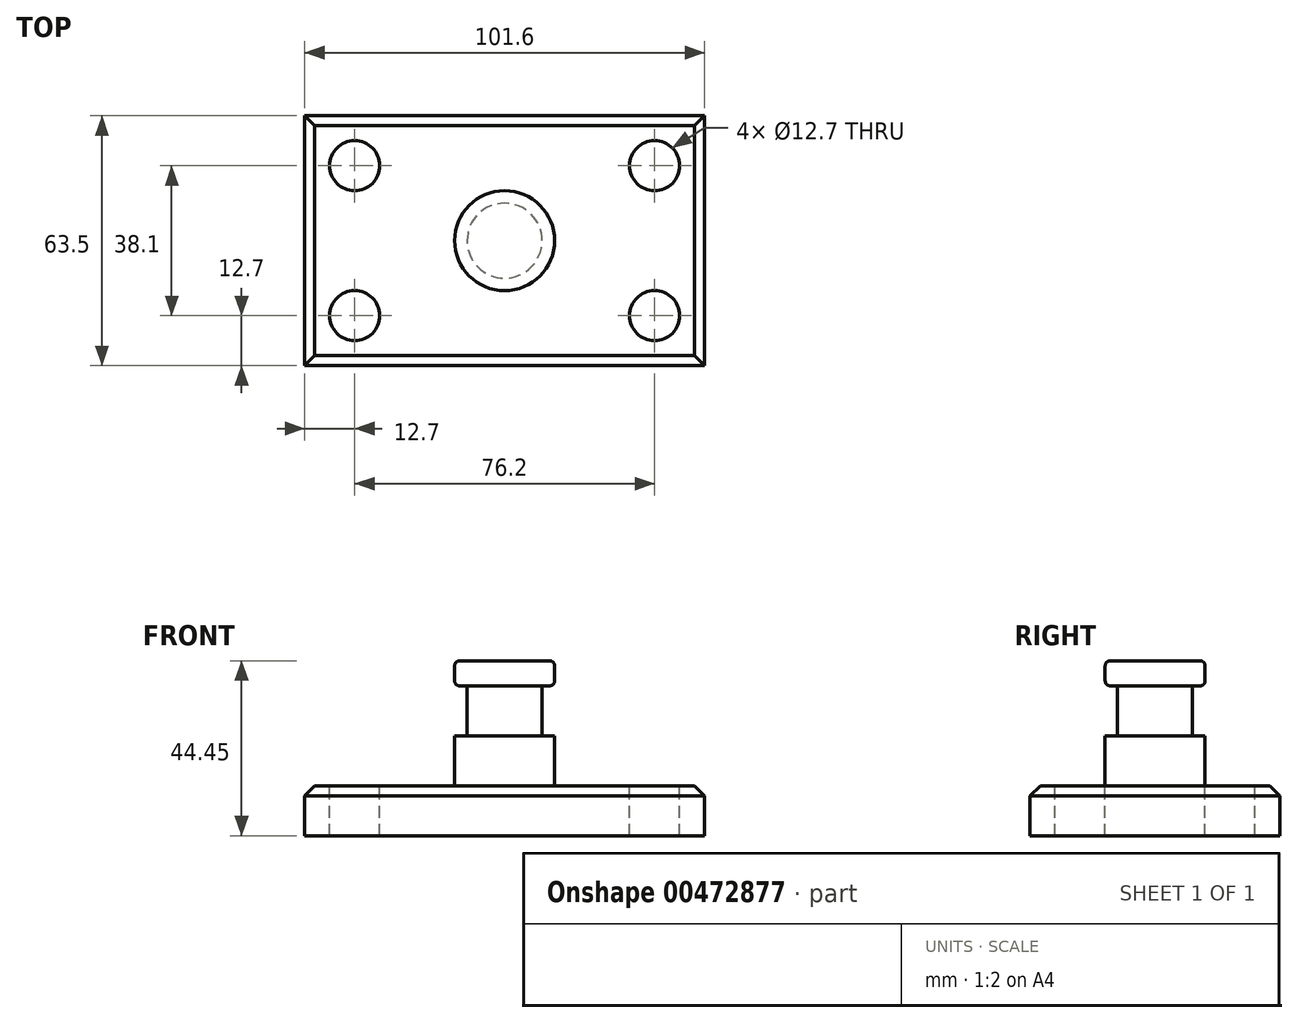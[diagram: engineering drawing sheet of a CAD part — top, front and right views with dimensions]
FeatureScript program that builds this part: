
annotation { "Feature Type Name" : "Feature", "Feature Type Description" : "" }
export const myFeature = defineFeature(function(context is Context, id is Id, definition is map)
    precondition{}
    {
        {
            var Q0;
            Q0=qCreatedBy(makeId("Top.planeOp"),FACE);
            var sketch = newSketch(context, id + "F0", { "sketchPlane" : qUnion([Q0])});
            skLineSegment(sketch, "E0.bottom", {"start": v(50.8, -31.75) * mm, "end": v(-50.8, -31.75) * mm});
            skLineSegment(sketch, "E0.top", {"start": v(50.8, 31.75) * mm, "end": v(-50.8, 31.75) * mm});
            skLineSegment(sketch, "E0.left", {"start": v(50.8, -31.75) * mm, "end": v(50.8, 31.75) * mm});
            skLineSegment(sketch, "E0.right", {"start": v(-50.8, -31.75) * mm, "end": v(-50.8, 31.75) * mm});
            skPoint(sketch, "E0.middle", {"position": v(0, 0) * mm});
            skSolve(sketch);
        }
        {
            var Q0;
            Q0=makeQuery(id+"F0.imprint","IMPRINT",FACE,{"disambiguationData":[TD([[makeQuery(id+"F0.imprint","IMPRINT",EDGE,{"derivedFrom":sQuery(id+"F0.wireOp",EDGE,"E0.bottom")}),-1.0]])]});
            extrude(context, id + "F1", {"entities" : qUnion([Q0]), "depth" : 12.7 * mm});
        }
        {
            var Q0;
            Q0=makeQuery(id+"F1.opExtrude","CAP_FACE",FACE,{"disambiguationData":[OSD([sQuery(id+"F0.wireOp",EDGE,"E0.bottom"),sQuery(id+"F0.wireOp",EDGE,"E0.top"),sQuery(id+"F0.wireOp",EDGE,"E0.left"),sQuery(id+"F0.wireOp",EDGE,"E0.right")])],"isStart":false});
            var sketch = newSketch(context, id + "F2", { "sketchPlane" : qUnion([Q0])});
            skCircle(sketch, "E1", {"center": v(-38.1, 19.05) * mm, "radius": 6.35 * mm});
            skCircle(sketch, "E2", {"center": v(-38.1, -19.05) * mm, "radius": 6.35 * mm});
            skCircle(sketch, "E3.MirrorC", {"center": v(38.1, 19.05) * mm, "radius": 6.35 * mm});
            skCircle(sketch, "E4.MirrorC", {"center": v(38.1, -19.05) * mm, "radius": 6.35 * mm});
            skSolve(sketch);
        }
        {
            var Q0;
            Q0 = qSketchRegion(id + "F2", true);
            extrude(context, id + "F3", {"entities" : qUnion([Q0]), "operationType" : NewBodyOperationType.REMOVE, "endBound" : BoundingType.THROUGH_ALL, "oppositeDirection" : true, "depth" : 25.4 * mm});
        }
        {
            var Q0;
            Q0=qCreatedBy(makeId("Front.planeOp"),FACE);
            var sketch = newSketch(context, id + "F4", { "sketchPlane" : qUnion([Q0])});
            skLineSegment(sketch, "E5.bottom", {"start": v(0, 12.7) * mm, "end": v(12.7, 12.7) * mm});
            skLineSegment(sketch, "E5.top", {"start": v(0, 44.45) * mm, "end": v(12.7, 44.45) * mm});
            skLineSegment(sketch, "E5.left", {"start": v(0, 12.7) * mm, "end": v(0, 44.45) * mm});
            skLineSegment(sketch, "E5.right", {"start": v(12.7, 12.7) * mm, "end": v(12.7, 44.45) * mm});
            skSolve(sketch);
        }
        {
            var Q0;
            Q0=makeQuery(id+"F4.imprint","IMPRINT",FACE,{"disambiguationData":[TD([[makeQuery(id+"F4.imprint","IMPRINT",EDGE,{"derivedFrom":sQuery(id+"F4.wireOp",EDGE,"E5.bottom")}),1.0]])]});
            var Q1;
            Q1=sQuery(id+"F4.wireOp",EDGE,"E5.left");
            revolve(context, id + "F5", {"operationType" : NewBodyOperationType.ADD, "entities" : qUnion([Q0]), "axis" : qUnion([Q1]), "revolveType" : RevolveType.FULL});
        }
        {
            var Q0;
            Q0=qCreatedBy(makeId("Front.planeOp"),FACE);
            var sketch = newSketch(context, id + "F6", { "sketchPlane" : qUnion([Q0])});
            skLineSegment(sketch, "E6.bottom", {"start": v(12.7, 38.1) * mm, "end": v(9.52, 38.1) * mm});
            skLineSegment(sketch, "E6.top", {"start": v(12.7, 25.4) * mm, "end": v(9.52, 25.4) * mm});
            skLineSegment(sketch, "E6.left", {"start": v(12.7, 38.1) * mm, "end": v(12.7, 25.4) * mm});
            skLineSegment(sketch, "E6.right", {"start": v(9.52, 38.1) * mm, "end": v(9.52, 25.4) * mm});
            skSolve(sketch);
        }
        {
            var Q0;
            Q0 = qSketchRegion(id + "F6", true);
            var Q1;
            Q1=sQuery(id+"F4.wireOp",EDGE,"E5.left");
            revolve(context, id + "F7", {"operationType" : NewBodyOperationType.REMOVE, "entities" : qUnion([Q0]), "axis" : qUnion([Q1]), "revolveType" : RevolveType.FULL, "oppositeDirection" : true});
        }
        {
            var Q0;
            Q0=makeQuery(id+"F5.opRevolve","SWEPT_EDGE",EDGE,{"disambiguationData":[OSD([sQuery(id+"F4.wireOp",EDGE,"E5.bottom"),sQuery(id+"F4.wireOp",EDGE,"E5.right")])]});
            var Q1;
            Q1=makeQuery(id+"F5.opRevolve","SWEPT_EDGE",EDGE,{"disambiguationData":[OSD([sQuery(id+"F4.wireOp",EDGE,"E5.top"),sQuery(id+"F4.wireOp",EDGE,"E5.right")])]});
            var Q2;
            Q2=makeQuery(id+"F7.boolean.opBoolean","COPY",EDGE,{"derivedFrom":makeQuery(id+"F7.opRevolve","SWEPT_EDGE",EDGE,{"disambiguationData":[OSD([sQuery(id+"F6.wireOp",EDGE,"E6.bottom"),sQuery(id+"F6.wireOp",EDGE,"E6.left")])]})});
            var Q3;
            Q3=makeQuery(id+"F7.boolean.opBoolean","COPY",EDGE,{"derivedFrom":makeQuery(id+"F7.opRevolve","SWEPT_EDGE",EDGE,{"disambiguationData":[OSD([sQuery(id+"F6.wireOp",EDGE,"E6.top"),sQuery(id+"F6.wireOp",EDGE,"E6.left")])]})});
            fillet(context, id + "F8", {"entities" : qUnion([Q0, Q1, Q2, Q3]), "radius" : 1.27 * mm, "tangentPropagation" : true, "allowEdgeOverflow" : false});
        }
        {
            var Q0;
            Q0=makeQuery(id+"F1.opExtrude","CAP_EDGE",EDGE,{"disambiguationData":[OSD([sQuery(id+"F0.wireOp",EDGE,"E0.bottom")])],"isStart":false});
            var Q1;
            Q1=makeQuery(id+"F1.opExtrude","CAP_EDGE",EDGE,{"disambiguationData":[OSD([sQuery(id+"F0.wireOp",EDGE,"E0.left")])],"isStart":false});
            var Q2;
            Q2=makeQuery(id+"F1.opExtrude","CAP_EDGE",EDGE,{"disambiguationData":[OSD([sQuery(id+"F0.wireOp",EDGE,"E0.top")])],"isStart":false});
            var Q3;
            Q3=makeQuery(id+"F1.opExtrude","CAP_EDGE",EDGE,{"disambiguationData":[OSD([sQuery(id+"F0.wireOp",EDGE,"E0.right")])],"isStart":false});
            chamfer(context, id + "F9", {"entities" : qUnion([Q0, Q1, Q2, Q3]), "width" : 2.54 * mm, "tangentPropagation" : true});
        }
    });
